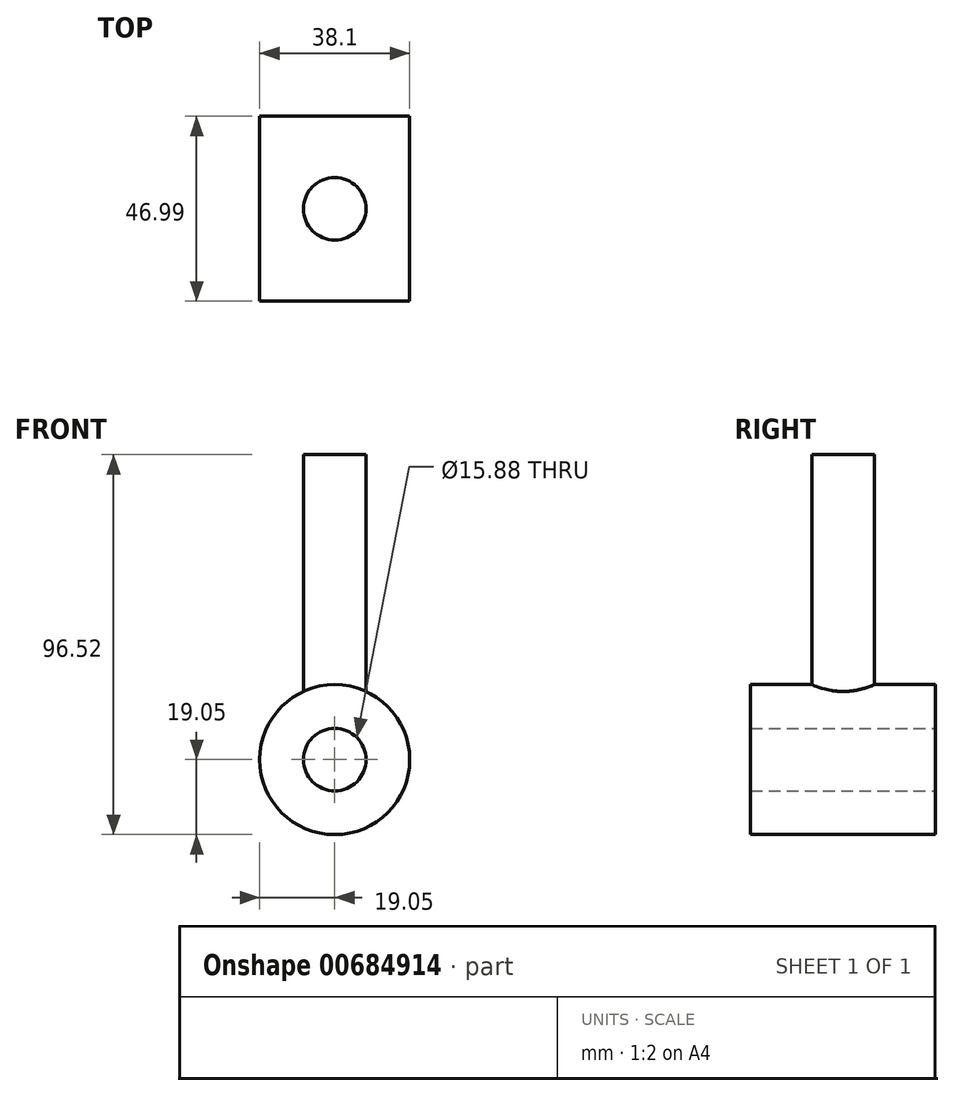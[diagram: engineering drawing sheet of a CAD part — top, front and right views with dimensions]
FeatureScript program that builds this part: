
annotation { "Feature Type Name" : "Feature", "Feature Type Description" : "" }
export const myFeature = defineFeature(function(context is Context, id is Id, definition is map)
    precondition{}
    {
        {
            var Q0;
            Q0=qCreatedBy(makeId("Front.planeOp"),FACE);
            var sketch = newSketch(context, id + "F0", { "sketchPlane" : qUnion([Q0])});
            skCircle(sketch, "E0", {"center": v(0, 0) * mm, "radius": 19.05 * mm});
            skCircle(sketch, "E1", {"center": v(0, 0) * mm, "radius": 7.94 * mm});
            skSolve(sketch);
        }
        {
            var Q0;
            Q0 = qSketchRegion(id + "F0", true);
            extrude(context, id + "F1", {"entities" : qUnion([Q0]), "depth" : 47 * mm, "offsetDistance" : 25.4 * mm});
        }
        {
            var Q0;
            Q0=qCreatedBy(makeId("Top.planeOp"),FACE);
            cPlane(context, id + "F2", {"entities" : qUnion([Q0]), "cplaneType" : CPlaneType.OFFSET, "offset" : 19.05 * mm, "width" : 152.4 * mm, "height" : 152.4 * mm});
        }
        {
            var Q0;
            Q0=qCreatedBy(id+"F2.planeOp",FACE);
            var sketch = newSketch(context, id + "F3", { "sketchPlane" : qUnion([Q0])});
            skLineSegment(sketch, "E2", {"start": v(0, 0) * mm, "end": v(0, -47) * mm, "construction": true});
            skCircle(sketch, "E3", {"center": v(0, -23.5) * mm, "radius": 7.94 * mm});
            skSolve(sketch);
        }
        {
            var Q0;
            Q0 = qSketchRegion(id + "F3", true);
            var Q1;
            Q1=makeQuery(id+"F1.opExtrude","SWEPT_FACE",FACE,{"disambiguationData":[OSD([sQuery(id+"F0.wireOp",EDGE,"E0")])]});
            extrude(context, id + "F4", {"entities" : qUnion([Q0]), "operationType" : NewBodyOperationType.ADD, "depth" : 58.42 * mm, "offsetDistance" : 25.4 * mm, "hasSecondDirection" : true, "secondDirectionBound" : BoundingType.UP_TO_SURFACE, "secondDirectionOppositeDirection" : true, "secondDirectionDepth" : 25.4 * mm, "secondDirectionBoundEntityFace" : qUnion([Q1])});
        }
    });
